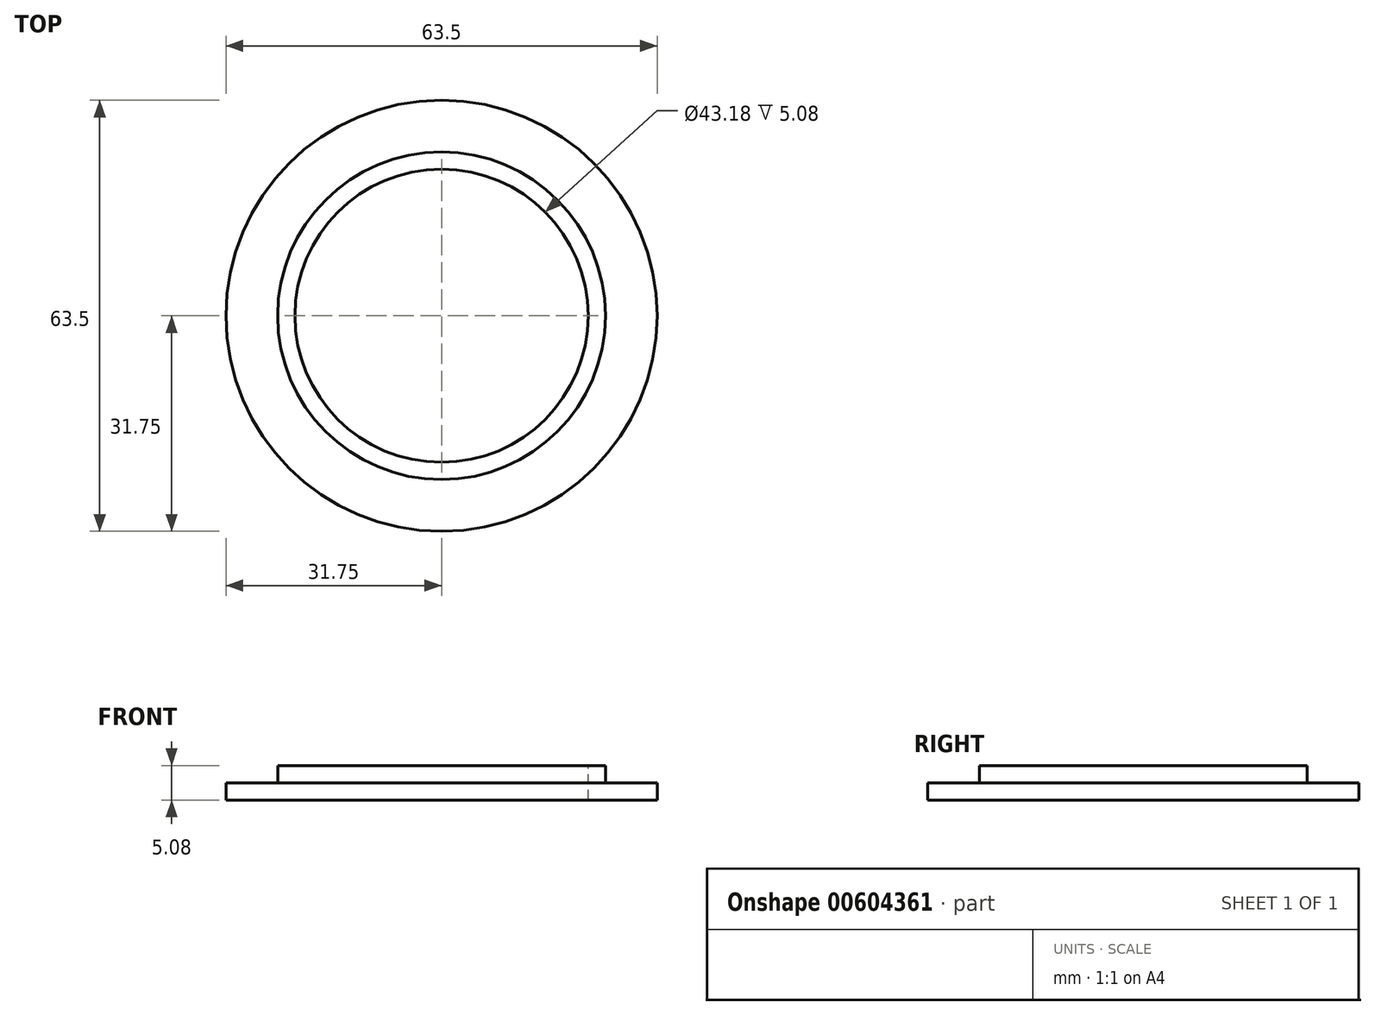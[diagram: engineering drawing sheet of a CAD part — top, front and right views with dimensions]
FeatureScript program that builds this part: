
annotation { "Feature Type Name" : "Feature", "Feature Type Description" : "" }
export const myFeature = defineFeature(function(context is Context, id is Id, definition is map)
    precondition{}
    {
        {
            var Q0;
            Q0=qCreatedBy(makeId("Front.planeOp"),FACE);
            var sketch = newSketch(context, id + "F0", { "sketchPlane" : qUnion([Q0])});
            skLineSegment(sketch, "E0", {"start": v(0, 16.47) * mm, "end": v(0, 0) * mm});
            skLineSegment(sketch, "E1", {"start": v(0, 0) * mm, "end": v(31.75, 0) * mm});
            skLineSegment(sketch, "E2", {"start": v(31.75, 0) * mm, "end": v(31.75, 2.54) * mm});
            skLineSegment(sketch, "E3", {"start": v(31.75, 2.54) * mm, "end": v(24.13, 2.54) * mm});
            skLineSegment(sketch, "E4", {"start": v(24.13, 2.54) * mm, "end": v(24.13, 5.08) * mm});
            skLineSegment(sketch, "E5", {"start": v(24.13, 5.08) * mm, "end": v(21.59, 5.08) * mm});
            skLineSegment(sketch, "E6", {"start": v(21.59, 5.08) * mm, "end": v(21.59, 0) * mm});
            skSolve(sketch);
        }
        {
            var Q0;
            {var subQ0=sQuery(id+"F0.wireOp",EDGE,"E2");Q0=makeQuery(id+"F0.imprint","IMPRINT",FACE,{"disambiguationData":[TD([[makeQuery(id+"F0.imprint","IMPRINT",EDGE,{"derivedFrom":subQ0}),1.0]])]});}
            var Q1;
            Q1=sQuery(id+"F0.wireOp",EDGE,"E0");
            revolve(context, id + "F1", {"entities" : qUnion([Q0]), "axis" : qUnion([Q1]), "revolveType" : RevolveType.FULL});
        }
    });
